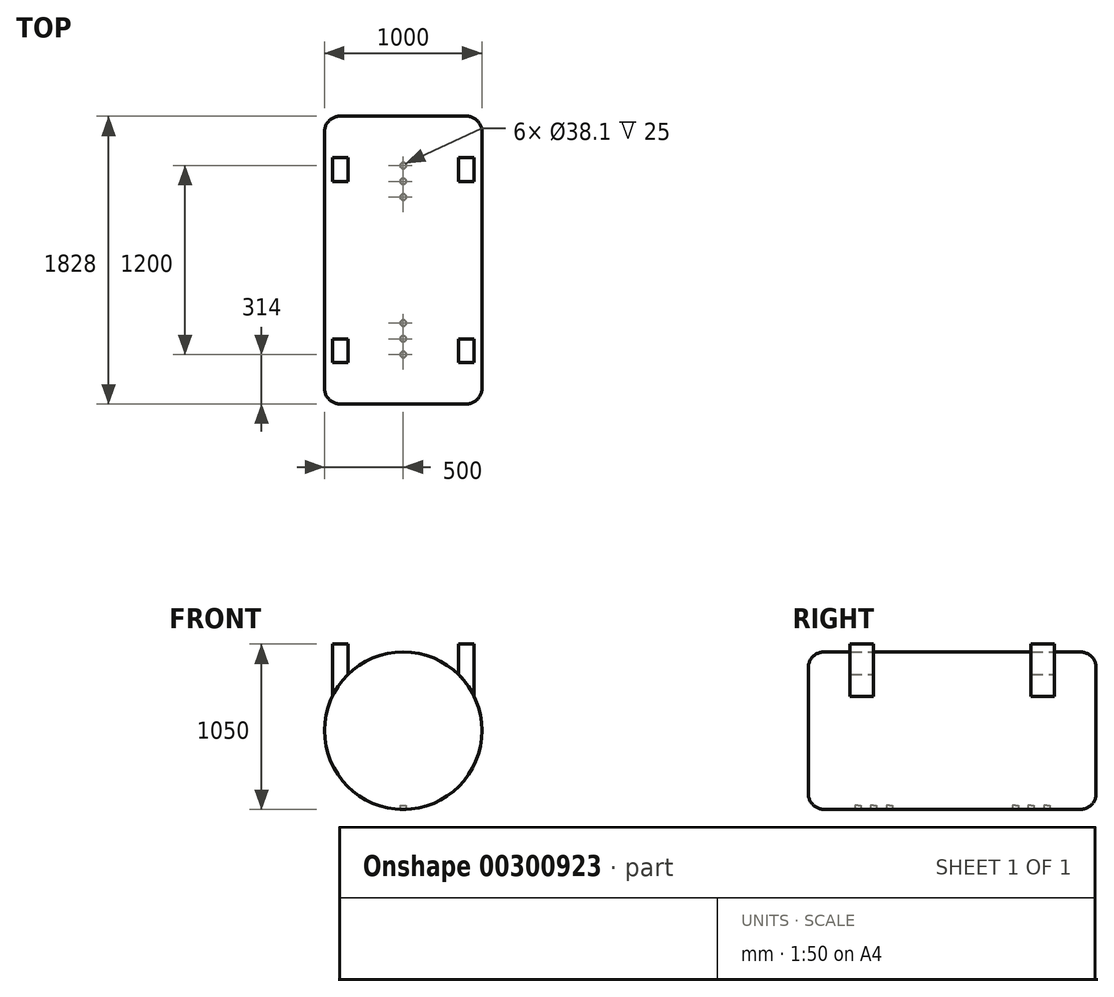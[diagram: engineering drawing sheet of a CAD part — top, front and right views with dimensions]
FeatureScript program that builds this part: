
annotation { "Feature Type Name" : "Feature", "Feature Type Description" : "" }
export const myFeature = defineFeature(function(context is Context, id is Id, definition is map)
    precondition{}
    {
        {
            var Q0;
            Q0=qCreatedBy(makeId("Front.planeOp"),FACE);
            var sketch = newSketch(context, id + "F0", { "sketchPlane" : qUnion([Q0])});
            skCircle(sketch, "E0", {"center": v(0, 0) * mm, "radius": 500 * mm});
            skSolve(sketch);
        }
        {
            var Q0;
            Q0=makeQuery(id+"F0.imprint","IMPRINT",FACE,{"disambiguationData":[TD([[makeQuery(id+"F0.imprint","IMPRINT",EDGE,{"derivedFrom":sQuery(id+"F0.wireOp",EDGE,"E0")}),1.0]])]});
            extrude(context, id + "F1", {"entities" : qUnion([Q0]), "depth" : 914 * mm, "hasSecondDirection" : true, "secondDirectionOppositeDirection" : true, "secondDirectionDepth" : 914 * mm});
        }
        {
            var Q0;
            Q0=makeQuery(id+"F1.opExtrude","CAP_EDGE",EDGE,{"disambiguationData":[OSD([sQuery(id+"F0.wireOp",EDGE,"E0")])],"isStart":false});
            var Q1;
            Q1=makeQuery(id+"F1.opExtrude","CAP_EDGE",EDGE,{"disambiguationData":[OSD([sQuery(id+"F0.wireOp",EDGE,"E0")])],"isStart":true});
            fillet(context, id + "F2", {"entities" : qUnion([Q0, Q1]), "radius" : 100 * mm, "tangentPropagation" : true, "allowEdgeOverflow" : false});
        }
        {
            var Q0;
            Q0=qCreatedBy(makeId("Top.planeOp"),FACE);
            cPlane(context, id + "F3", {"entities" : qUnion([Q0]), "cplaneType" : CPlaneType.OFFSET, "offset" : 500 * mm, "width" : 150 * mm, "height" : 150 * mm});
        }
        {
            var Q0;
            Q0=qCreatedBy(id+"F3.planeOp",FACE);
            var sketch = newSketch(context, id + "F4", { "sketchPlane" : qUnion([Q0])});
            skLineSegment(sketch, "E1.bottom", {"start": v(-450, 650) * mm, "end": v(-350, 650) * mm});
            skLineSegment(sketch, "E1.top", {"start": v(-450, 500) * mm, "end": v(-350, 500) * mm});
            skLineSegment(sketch, "E1.left", {"start": v(-450, 650) * mm, "end": v(-450, 500) * mm});
            skLineSegment(sketch, "E1.right", {"start": v(-350, 650) * mm, "end": v(-350, 500) * mm});
            skLineSegment(sketch, "E2", {"start": v(0, 193.18) * mm, "end": v(0, -109.1) * mm, "construction": true});
            skLineSegment(sketch, "E3", {"start": v(-255.77, 0) * mm, "end": v(349.78, 0) * mm, "construction": true});
            skLineSegment(sketch, "E4.MirrorCS", {"start": v(450, 650) * mm, "end": v(350, 650) * mm});
            skLineSegment(sketch, "E5.MirrorCS", {"start": v(450, 500) * mm, "end": v(350, 500) * mm});
            skLineSegment(sketch, "E6.MirrorCS", {"start": v(350, 650) * mm, "end": v(350, 500) * mm});
            skLineSegment(sketch, "E7.MirrorCS", {"start": v(450, 650) * mm, "end": v(450, 500) * mm});
            skLineSegment(sketch, "E8.MirrorCS", {"start": v(350, -650) * mm, "end": v(350, -500) * mm});
            skLineSegment(sketch, "E9.MirrorCS", {"start": v(450, -500) * mm, "end": v(350, -500) * mm});
            skLineSegment(sketch, "E10.MirrorCS", {"start": v(450, -650) * mm, "end": v(450, -500) * mm});
            skLineSegment(sketch, "E11.MirrorCS", {"start": v(450, -650) * mm, "end": v(350, -650) * mm});
            skLineSegment(sketch, "E12.MirrorCS", {"start": v(-450, -650) * mm, "end": v(-350, -650) * mm});
            skLineSegment(sketch, "E13.MirrorCS", {"start": v(-450, -650) * mm, "end": v(-450, -500) * mm});
            skLineSegment(sketch, "E14.MirrorCS", {"start": v(-450, -500) * mm, "end": v(-350, -500) * mm});
            skLineSegment(sketch, "E15.MirrorCS", {"start": v(-350, -650) * mm, "end": v(-350, -500) * mm});
            skSolve(sketch);
        }
        {
            var Q0;
            Q0=makeQuery(id+"F4.imprint","IMPRINT",FACE,{"disambiguationData":[TD([[makeQuery(id+"F4.imprint","IMPRINT",EDGE,{"derivedFrom":sQuery(id+"F4.wireOp",EDGE,"E1.bottom")}),-1.0]])]});
            var Q1;
            Q1=makeQuery(id+"F4.imprint","IMPRINT",FACE,{"disambiguationData":[TD([[makeQuery(id+"F4.imprint","IMPRINT",EDGE,{"derivedFrom":sQuery(id+"F4.wireOp",EDGE,"E4.MirrorCS")}),1.0]])]});
            var Q2;
            Q2=makeQuery(id+"F4.imprint","IMPRINT",FACE,{"disambiguationData":[TD([[makeQuery(id+"F4.imprint","IMPRINT",EDGE,{"derivedFrom":sQuery(id+"F4.wireOp",EDGE,"E8.MirrorCS")}),-1.0]])]});
            var Q3;
            Q3=makeQuery(id+"F4.imprint","IMPRINT",FACE,{"disambiguationData":[TD([[makeQuery(id+"F4.imprint","IMPRINT",EDGE,{"derivedFrom":sQuery(id+"F4.wireOp",EDGE,"E12.MirrorCS")}),1.0]])]});
            var Q4;
            Q4=makeQuery(id+"F1.opExtrude","SWEPT_FACE",FACE,{"disambiguationData":[OSD([sQuery(id+"F0.wireOp",EDGE,"E0")])]});
            extrude(context, id + "F5", {"entities" : qUnion([Q0, Q1, Q2, Q3]), "operationType" : NewBodyOperationType.ADD, "endBound" : BoundingType.UP_TO_SURFACE, "oppositeDirection" : true, "endBoundEntityFace" : qUnion([Q4]), "depth" : 25 * mm, "hasSecondDirection" : true, "secondDirectionOppositeDirection" : false, "secondDirectionDepth" : 50 * mm});
        }
        {
            var Q0;
            Q0=qCreatedBy(makeId("Top.planeOp"),FACE);
            cPlane(context, id + "F6", {"entities" : qUnion([Q0]), "cplaneType" : CPlaneType.OFFSET, "offset" : 500 * mm, "oppositeDirection" : true, "width" : 150 * mm, "height" : 150 * mm});
        }
        {
            var Q0;
            Q0=qCreatedBy(id+"F6.planeOp",FACE);
            var sketch = newSketch(context, id + "F7", { "sketchPlane" : qUnion([Q0])});
            skCircle(sketch, "E16", {"center": v(0, -600) * mm, "radius": 19.05 * mm});
            skCircle(sketch, "E17", {"center": v(0, -500) * mm, "radius": 19.05 * mm});
            skCircle(sketch, "E18", {"center": v(0, -400) * mm, "radius": 19.05 * mm});
            skCircle(sketch, "E19", {"center": v(0, 500) * mm, "radius": 19.05 * mm});
            skCircle(sketch, "E20", {"center": v(0, 400) * mm, "radius": 19.05 * mm});
            skCircle(sketch, "E21", {"center": v(0, 600) * mm, "radius": 19.05 * mm});
            skSolve(sketch);
        }
        {
            var Q0;
            Q0 = qSketchRegion(id + "F7", true);
            extrude(context, id + "F8", {"entities" : qUnion([Q0]), "operationType" : NewBodyOperationType.REMOVE, "depth" : 25 * mm});
        }
    });
